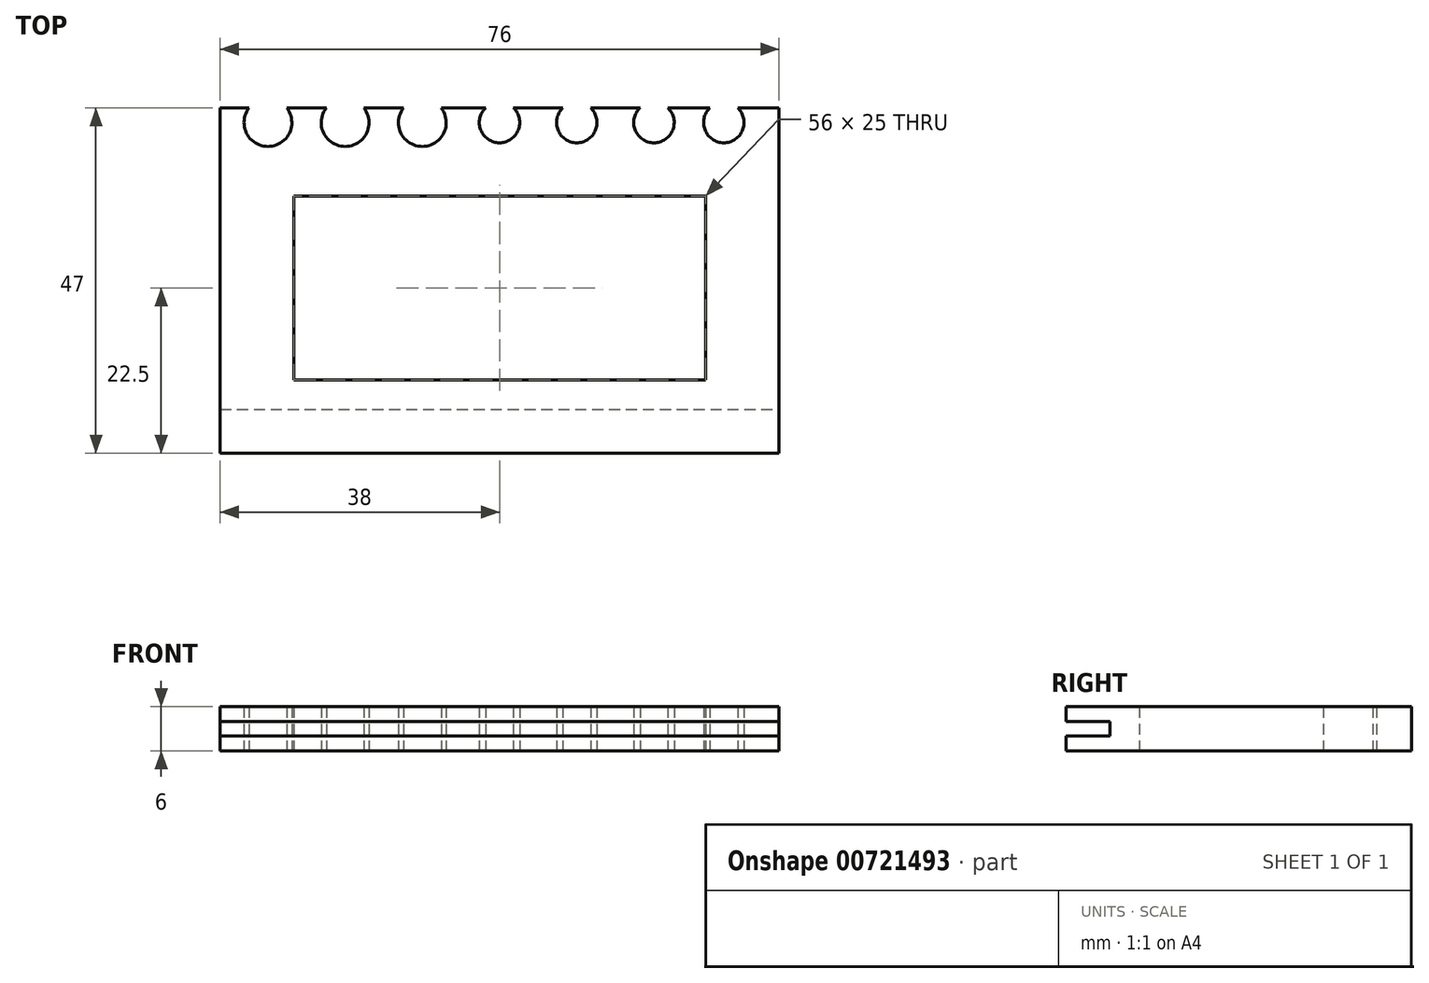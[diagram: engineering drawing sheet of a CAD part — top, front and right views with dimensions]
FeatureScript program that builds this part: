
annotation { "Feature Type Name" : "Feature", "Feature Type Description" : "" }
export const myFeature = defineFeature(function(context is Context, id is Id, definition is map)
    precondition{}
    {
        {
            var Q0;
            Q0=qCreatedBy(makeId("Top.planeOp"),FACE);
            var sketch = newSketch(context, id + "F0", { "sketchPlane" : qUnion([Q0])});
            skArc(sketch, "E0", {"start": v(-1.89, 2) * mm, "mid": v(0, -2.75) * mm, "end": v(1.89, 2) * mm});
            skArc(sketch, "E1", {"start": v(-3.17, 2) * mm, "mid": v(-3.6, 1.04) * mm, "end": v(-3.75, 0) * mm});
            skLineSegment(sketch, "E2.bottom", {"start": v(-2.75, 0) * mm, "end": v(-7.75, 0) * mm});
            skLineSegment(sketch, "E2.top", {"start": v(0, -45) * mm, "end": v(-38, -45) * mm});
            skLineSegment(sketch, "E2.left", {"start": v(0, -2.75) * mm, "end": v(0, -45) * mm});
            skLineSegment(sketch, "E2.right", {"start": v(-38, 0) * mm, "end": v(-38, -45) * mm});
            skLineSegment(sketch, "E3.top", {"start": v(-38, 5.1) * mm, "end": v(5.33, 5.1) * mm, "construction": true});
            skLineSegment(sketch, "E3.left", {"start": v(-38, 2) * mm, "end": v(-38, 5.1) * mm, "construction": true});
            skLineSegment(sketch, "E3.right", {"start": v(5.33, 2) * mm, "end": v(5.33, 5.1) * mm, "construction": true});
            skLineSegment(sketch, "E4", {"start": v(-33.67, 2) * mm, "end": v(-32.39, 2) * mm});
            skLineSegment(sketch, "E5.trimOffspring", {"start": v(-28.61, 2) * mm, "end": v(-27.33, 2) * mm});
            skLineSegment(sketch, "E6.trimOffspring", {"start": v(-24.17, 2) * mm, "end": v(-22.89, 2) * mm});
            skLineSegment(sketch, "E7.trimOffspring", {"start": v(-18.44, 2) * mm, "end": v(-17.83, 2) * mm});
            skLineSegment(sketch, "E8.trimOffspring", {"start": v(-13.67, 2) * mm, "end": v(-13.06, 2) * mm});
            skLineSegment(sketch, "E9.trimOffspring", {"start": v(-7.94, 2) * mm, "end": v(-7.33, 2) * mm});
            skLineSegment(sketch, "E10.trimOffspring", {"start": v(-3.17, 2) * mm, "end": v(-1.89, 2) * mm});
            skLineSegment(sketch, "E11.trimOffspring", {"start": v(1.89, 2) * mm, "end": v(3.17, 2) * mm});
            skLineSegment(sketch, "E12.trimOffspring", {"start": v(-33.25, 0) * mm, "end": v(-38, 0) * mm});
            skLineSegment(sketch, "E13.trimOffspring", {"start": v(-25, 0) * mm, "end": v(-27.75, 0) * mm});
            skLineSegment(sketch, "E14.trimOffspring", {"start": v(-13.25, 0) * mm, "end": v(-17.25, 0) * mm});
            skLineSegment(sketch, "E15.MirrorCS", {"start": v(8.61, 2) * mm, "end": v(7.33, 2) * mm});
            skLineSegment(sketch, "E16.MirrorCS", {"start": v(-1.89, 2) * mm, "end": v(-3.17, 2) * mm});
            skLineSegment(sketch, "E17.MirrorCS", {"start": v(24.17, 2) * mm, "end": v(22.89, 2) * mm});
            skLineSegment(sketch, "E18.MirrorCS", {"start": v(13.67, 2) * mm, "end": v(12.39, 2) * mm});
            skLineSegment(sketch, "E19.MirrorCS", {"start": v(33.67, 2) * mm, "end": v(32.39, 2) * mm});
            skLineSegment(sketch, "E20.MirrorCS", {"start": v(3.17, 2) * mm, "end": v(1.89, 2) * mm});
            skLineSegment(sketch, "E21.MirrorCS", {"start": v(19.11, 2) * mm, "end": v(17.83, 2) * mm});
            skLineSegment(sketch, "E22.MirrorCS", {"start": v(28.61, 2) * mm, "end": v(27.33, 2) * mm});
            skLineSegment(sketch, "E23.MirrorCS", {"start": v(-5.33, 2) * mm, "end": v(-5.33, 5.1) * mm, "construction": true});
            skLineSegment(sketch, "E24.MirrorCS", {"start": v(38, 2) * mm, "end": v(38, 5.1) * mm, "construction": true});
            skLineSegment(sketch, "E25.MirrorCS", {"start": v(33.25, 0) * mm, "end": v(38, 0) * mm});
            skArc(sketch, "E26.MirrorCS", {"start": v(3.17, 2) * mm, "mid": v(0, -3.75) * mm, "end": v(-3.17, 2) * mm});
            skArc(sketch, "E27.MirrorCS", {"start": v(22.89, 2) * mm, "mid": v(21, -2.75) * mm, "end": v(19.11, 2) * mm});
            skArc(sketch, "E28.MirrorCS", {"start": v(17.25, 0) * mm, "mid": v(17.4, 1.04) * mm, "end": v(17.83, 2) * mm});
            skLineSegment(sketch, "E29.MirrorCS", {"start": v(13.25, 0) * mm, "end": v(17.25, 0) * mm});
            skLineSegment(sketch, "E30.MirrorCS", {"start": v(2.75, 0) * mm, "end": v(7.75, 0) * mm});
            skArc(sketch, "E31.MirrorCS", {"start": v(1.89, 2) * mm, "mid": v(0, -2.75) * mm, "end": v(-1.89, 2) * mm});
            skLineSegment(sketch, "E32.MirrorCS", {"start": v(38, 5.1) * mm, "end": v(-5.33, 5.1) * mm, "construction": true});
            skArc(sketch, "E33.MirrorCS", {"start": v(13.67, 2) * mm, "mid": v(14.1, 1.04) * mm, "end": v(14.25, 0) * mm});
            skArc(sketch, "E34.MirrorCS", {"start": v(12.39, 2) * mm, "mid": v(10.5, -2.75) * mm, "end": v(8.61, 2) * mm});
            skLineSegment(sketch, "E35.MirrorCS", {"start": v(25, 0) * mm, "end": v(27.75, 0) * mm});
            skArc(sketch, "E36.MirrorCS", {"start": v(32.39, 2) * mm, "mid": v(30.5, -2.75) * mm, "end": v(28.61, 2) * mm});
            skArc(sketch, "E37.MirrorCS", {"start": v(33.67, 2) * mm, "mid": v(34.1, 1.04) * mm, "end": v(34.25, 0) * mm});
            skLineSegment(sketch, "E38.MirrorCS", {"start": v(38, 0) * mm, "end": v(38, -45) * mm});
            skLineSegment(sketch, "E39.MirrorCS", {"start": v(0, -45) * mm, "end": v(38, -45) * mm});
            skLineSegment(sketch, "E40.bottom", {"start": v(-28, -35) * mm, "end": v(28, -35) * mm});
            skLineSegment(sketch, "E40.top", {"start": v(-28, -10) * mm, "end": v(28, -10) * mm});
            skLineSegment(sketch, "E40.left", {"start": v(-28, -35) * mm, "end": v(-28, -10) * mm});
            skLineSegment(sketch, "E40.right", {"start": v(28, -35) * mm, "end": v(28, -10) * mm});
            skLineSegment(sketch, "E41.bottom", {"start": v(-38, 0) * mm, "end": v(-34.75, 0) * mm});
            skLineSegment(sketch, "E41.top", {"start": v(-38, 2) * mm, "end": v(-33.67, 2) * mm});
            skLineSegment(sketch, "E41.left", {"start": v(-38, 0) * mm, "end": v(-38, 2) * mm});
            skLineSegment(sketch, "E41.right", {"start": v(38, 0) * mm, "end": v(38, 2) * mm});
            skPoint(sketch, "E42.center.orphan", {"position": v(-21, 0) * mm});
            skPoint(sketch, "E43.center.orphan", {"position": v(-10.5, 0) * mm});
            skLineSegment(sketch, "E44.trimOffspring", {"start": v(1.89, 2) * mm, "end": v(8.61, 2) * mm});
            skLineSegment(sketch, "E45.trimOffspring", {"start": v(22.89, 2) * mm, "end": v(28.61, 2) * mm});
            skLineSegment(sketch, "E46.trimOffspring", {"start": v(32.39, 2) * mm, "end": v(38, 2) * mm});
            skLineSegment(sketch, "E47.trimOffspring", {"start": v(13.25, 0) * mm, "end": v(18.25, 0) * mm});
            skLineSegment(sketch, "E48.trimOffspring", {"start": v(12.39, 2) * mm, "end": v(19.11, 2) * mm});
            skArc(sketch, "E49", {"start": v(-13.06, 2) * mm, "mid": v(-10.5, -3.25) * mm, "end": v(-7.94, 2) * mm});
            skArc(sketch, "E50", {"start": v(-14.25, 2) * mm, "mid": v(-14.62, 1.03) * mm, "end": v(-14.75, 0) * mm});
            skLineSegment(sketch, "E51.trimOffspring", {"start": v(-7.94, 2) * mm, "end": v(-3.17, 2) * mm});
            skLineSegment(sketch, "E52.trimOffspring", {"start": v(-7.25, 0) * mm, "end": v(-2.75, 0) * mm});
            skPoint(sketch, "E53.orphan", {"position": v(-8.61, 2) * mm});
            skArc(sketch, "E54", {"start": v(-23.56, 2) * mm, "mid": v(-21, -3.25) * mm, "end": v(-18.44, 2) * mm});
            skArc(sketch, "E55", {"start": v(-24.75, 2) * mm, "mid": v(-25.12, 1.03) * mm, "end": v(-25.25, 0) * mm});
            skLineSegment(sketch, "E56.trimOffspring", {"start": v(-19.11, 2) * mm, "end": v(-13.06, 2) * mm});
            skLineSegment(sketch, "E57.trimOffspring", {"start": v(-17.75, 0) * mm, "end": v(-13.75, 0) * mm});
            skPoint(sketch, "E58.orphan", {"position": v(-12.39, 2) * mm});
            skArc(sketch, "E59", {"start": v(-34.06, 2) * mm, "mid": v(-31.5, -3.25) * mm, "end": v(-28.94, 2) * mm});
            skLineSegment(sketch, "E60.trimOffspring", {"start": v(-28.94, 2) * mm, "end": v(-23.56, 2) * mm});
            skLineSegment(sketch, "E61.trimOffspring", {"start": v(-28.25, 0) * mm, "end": v(-25, 0) * mm});
            skArc(sketch, "E62.trimOffspring", {"start": v(-16.75, 0) * mm, "mid": v(-16.88, 1.03) * mm, "end": v(-17.25, 2) * mm});
            skArc(sketch, "E63.trimOffspring", {"start": v(-6.25, 0) * mm, "mid": v(-6.38, 1.03) * mm, "end": v(-6.75, 2) * mm});
            skArc(sketch, "E64.trimOffspring", {"start": v(3.75, 0) * mm, "mid": v(3.6, 1.04) * mm, "end": v(3.17, 2) * mm});
            skArc(sketch, "E65.trimOffspring", {"start": v(6.75, 0) * mm, "mid": v(6.9, 1.04) * mm, "end": v(7.33, 2) * mm});
            skArc(sketch, "E66.trimOffspring", {"start": v(26.75, 0) * mm, "mid": v(26.9, 1.04) * mm, "end": v(27.33, 2) * mm});
            skSolve(sketch);
        }
        {
            var Q0;
            Q0 = qSketchRegion(id + "F0", true);
            extrude(context, id + "F1", {"entities" : qUnion([Q0]), "depth" : 3 * mm, "offsetDistance" : 25 * mm, "hasSecondDirection" : true, "secondDirectionOppositeDirection" : true, "secondDirectionDepth" : 3 * mm});
        }
        {
            var Q0;
            Q0=makeQuery(id+"F1.opExtrude","SWEPT_FACE",FACE,{"disambiguationData":[OSD([sQuery(id+"F0.wireOp",EDGE,"E2.top"),sQuery(id+"F0.wireOp",EDGE,"E39.MirrorCS")])]});
            var sketch = newSketch(context, id + "F2", { "sketchPlane" : qUnion([Q0])});
            skLineSegment(sketch, "E67.bottom", {"start": v(-52.7, 1) * mm, "end": v(52.7, 1) * mm});
            skLineSegment(sketch, "E67.top", {"start": v(-52.7, -1) * mm, "end": v(52.7, -1) * mm});
            skLineSegment(sketch, "E67.left", {"start": v(-52.7, 1) * mm, "end": v(-52.7, -1) * mm});
            skLineSegment(sketch, "E67.right", {"start": v(52.7, 1) * mm, "end": v(52.7, -1) * mm});
            skPoint(sketch, "E67.middle", {"position": v(0, 0) * mm});
            skSolve(sketch);
        }
        {
            var Q0;
            Q0 = qSketchRegion(id + "F2", true);
            extrude(context, id + "F3", {"entities" : qUnion([Q0]), "operationType" : NewBodyOperationType.REMOVE, "oppositeDirection" : true, "depth" : 6 * mm, "offsetDistance" : 25 * mm});
        }
    });
